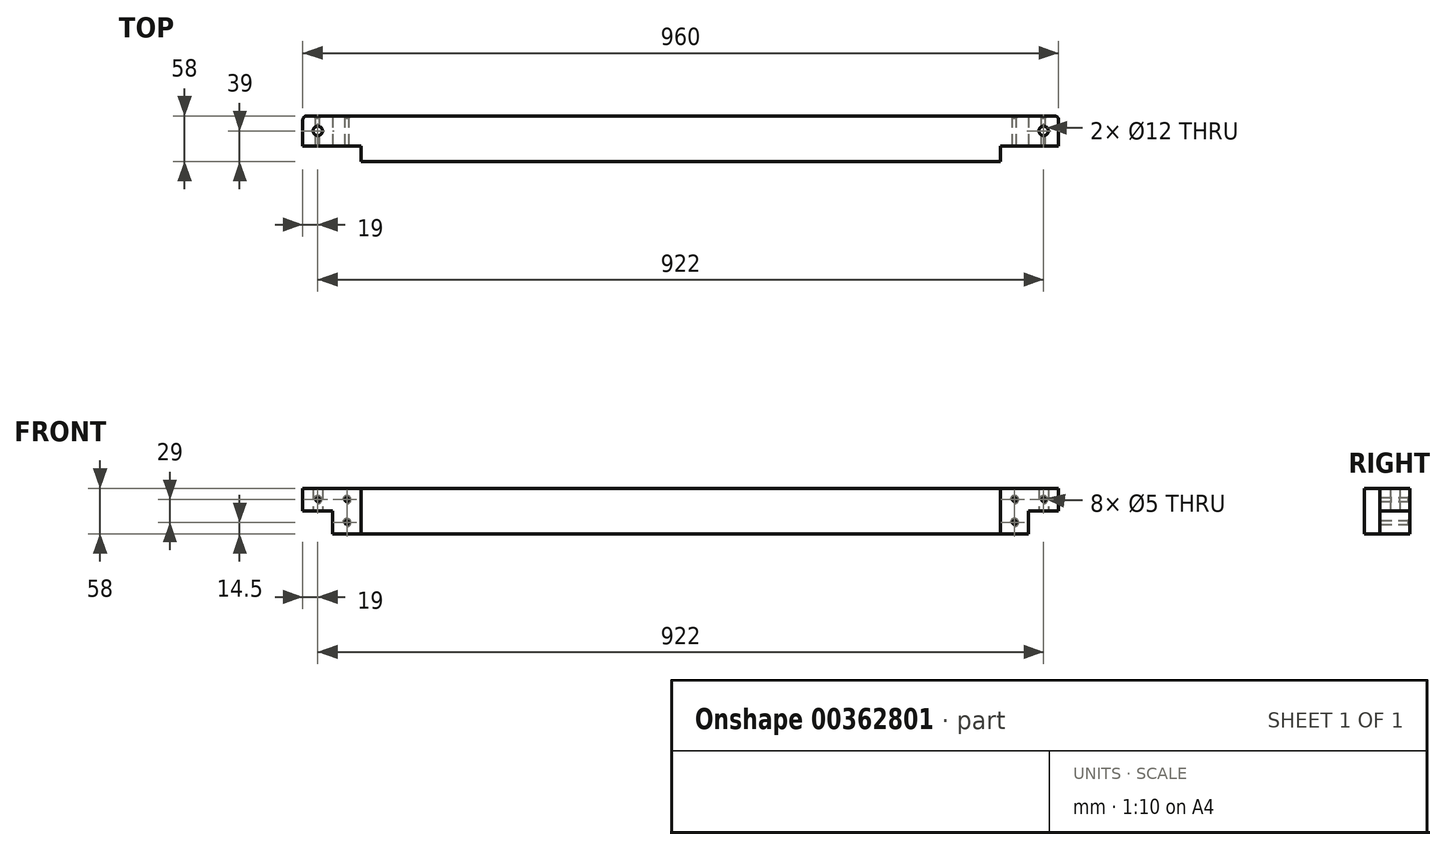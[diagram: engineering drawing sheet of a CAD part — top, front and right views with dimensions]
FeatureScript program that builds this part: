
annotation { "Feature Type Name" : "Feature", "Feature Type Description" : "" }
export const myFeature = defineFeature(function(context is Context, id is Id, definition is map)
    precondition{}
    {
        {
            var Q0;
            Q0=qCreatedBy(makeId("Right.planeOp"),FACE);
            var sketch = newSketch(context, id + "F0", { "sketchPlane" : qUnion([Q0])});
            skLineSegment(sketch, "E0.bottom", {"start": v(29, 29) * mm, "end": v(-29, 29) * mm});
            skLineSegment(sketch, "E0.top", {"start": v(29, -29) * mm, "end": v(-29, -29) * mm});
            skLineSegment(sketch, "E0.left", {"start": v(29, 29) * mm, "end": v(29, -29) * mm});
            skLineSegment(sketch, "E0.right", {"start": v(-29, 29) * mm, "end": v(-29, -29) * mm});
            skPoint(sketch, "E0.middle", {"position": v(0, 0) * mm});
            skLineSegment(sketch, "E1", {"start": v(-9, 29) * mm, "end": v(-9, -29) * mm});
            skLineSegment(sketch, "E2", {"start": v(29, 0) * mm, "end": v(-9, 0) * mm});
            skSolve(sketch);
        }
        {
            var Q0;
            {var subQ5=sQuery(id+"F0.wireOp",EDGE,"E2");Q0=makeQuery(id+"F0.imprint","IMPRINT",FACE,{"disambiguationData":[TD([[makeQuery(id+"F0.imprint","IMPRINT",EDGE,{"derivedFrom":subQ5}),1.0]])]});}
            var Q1;
            {var subQ5=sQuery(id+"F0.wireOp",EDGE,"E2");Q1=makeQuery(id+"F0.imprint","IMPRINT",FACE,{"disambiguationData":[TD([[makeQuery(id+"F0.imprint","IMPRINT",EDGE,{"derivedFrom":subQ5}),-1.0]])]});}
            var Q2;
            {var subQ4=sQuery(id+"F0.wireOp",EDGE,"E0.right");Q2=makeQuery(id+"F0.imprint","IMPRINT",FACE,{"disambiguationData":[TD([[makeQuery(id+"F0.imprint","IMPRINT",EDGE,{"derivedFrom":subQ4}),1.0]])]});}
            extrude(context, id + "F1", {"entities" : qUnion([Q0, Q1, Q2]), "oppositeDirection" : true, "depth" : 480 * mm});
        }
        {
            var Q0;
            {var subQ4=sQuery(id+"F0.wireOp",EDGE,"E0.right");Q0=makeQuery(id+"F0.imprint","IMPRINT",FACE,{"disambiguationData":[TD([[makeQuery(id+"F0.imprint","IMPRINT",EDGE,{"derivedFrom":subQ4}),1.0]])]});}
            extrude(context, id + "F2", {"entities" : qUnion([Q0]), "operationType" : NewBodyOperationType.REMOVE, "oppositeDirection" : true, "depth" : 74 * mm});
        }
        {
            var Q0;
            {var subQ5=sQuery(id+"F0.wireOp",EDGE,"E2");Q0=makeQuery(id+"F0.imprint","IMPRINT",FACE,{"disambiguationData":[TD([[makeQuery(id+"F0.imprint","IMPRINT",EDGE,{"derivedFrom":subQ5}),1.0]])]});}
            extrude(context, id + "F3", {"entities" : qUnion([Q0]), "operationType" : NewBodyOperationType.REMOVE, "oppositeDirection" : true, "depth" : 38 * mm});
        }
        {
            var Q0;
            Q0=makeQuery(id+"F1.opExtrude","CAP_EDGE",EDGE,{"disambiguationData":[OSD([sQuery(id+"F0.wireOp",EDGE,"E0.left")])],"isStart":true});
            fillet(context, id + "F4", {"entities" : qUnion([Q0]), "radius" : 5 * mm, "tangentPropagation" : true, "allowEdgeOverflow" : false});
        }
        {
            var Q0;
            Q0=makeQuery(id+"F3.boolean.opBoolean","COPY",FACE,{"derivedFrom":makeQuery(id+"F3.opExtrude","SWEPT_FACE",FACE,{"disambiguationData":[OSD([sQuery(id+"F0.wireOp",EDGE,"E2")])]})});
            var sketch = newSketch(context, id + "F5", { "sketchPlane" : qUnion([Q0])});
            skPoint(sketch, "E3", {"position": v(-19, -10) * mm});
            skSolve(sketch);
        }
        {
            var Q0;
            Q0=makeQuery(id+"F1.opExtrude","SWEPT_FACE",FACE,{"disambiguationData":[OSD([sQuery(id+"F0.wireOp",EDGE,"E0.left")])]});
            var sketch = newSketch(context, id + "F6", { "sketchPlane" : qUnion([Q0])});
            skPoint(sketch, "E4", {"position": v(19, 14.5) * mm});
            skPoint(sketch, "E5", {"position": v(56, 14.5) * mm});
            skPoint(sketch, "E6", {"position": v(56, -14.5) * mm});
            skSolve(sketch);
        }
        {
            var Q0;
            Q0=sQuery(id+"F5.wireOp",VERTEX,"E3");
            var Q1;
            Q1=makeQuery(id+"F1.opExtrude","SWEPT_BODY",BODY,{"disambiguationData":[OSD([sQuery(id+"F0.wireOp",EDGE,"E0.bottom"),sQuery(id+"F0.wireOp",EDGE,"E0.top"),sQuery(id+"F0.wireOp",EDGE,"E0.left"),sQuery(id+"F0.wireOp",EDGE,"E0.right")])]});
            hole(context, id + "F7", {"style" : HoleStyle.SIMPLE, "endStyle" : HoleEndStyle.THROUGH, "holeDiameter" : 12 * mm, "isTappedThrough" : true, "tappedDepth" : 12 * mm, "tapClearance" : 3, "locations" : qUnion([Q0]), "scope" : qUnion([Q1])});
        }
        {
            var Q0;
            Q0=sQuery(id+"F6.wireOp",VERTEX,"E4");
            var Q1;
            Q1=sQuery(id+"F6.wireOp",VERTEX,"E5");
            var Q2;
            Q2=sQuery(id+"F6.wireOp",VERTEX,"E6");
            var Q3;
            Q3=makeQuery(id+"F1.opExtrude","SWEPT_BODY",BODY,{"disambiguationData":[OSD([sQuery(id+"F0.wireOp",EDGE,"E0.bottom"),sQuery(id+"F0.wireOp",EDGE,"E0.top"),sQuery(id+"F0.wireOp",EDGE,"E0.left"),sQuery(id+"F0.wireOp",EDGE,"E0.right")])]});
            hole(context, id + "F8", {"style" : HoleStyle.C_SINK, "endStyle" : HoleEndStyle.THROUGH, "holeDiameter" : 5 * mm, "cSinkDiameter" : 10 * mm, "cSinkAngle" : 90 * degree, "isTappedThrough" : true, "tappedDepth" : 12 * mm, "tapClearance" : 3, "locations" : qUnion([Q0, Q1, Q2]), "scope" : qUnion([Q3])});
        }
        {
            var Q0;
            Q0=makeQuery(id+"F1.opExtrude","SWEPT_BODY",BODY,{"disambiguationData":[OSD([sQuery(id+"F0.wireOp",EDGE,"E0.bottom"),sQuery(id+"F0.wireOp",EDGE,"E0.top"),sQuery(id+"F0.wireOp",EDGE,"E0.left"),sQuery(id+"F0.wireOp",EDGE,"E0.right")])]});
            var Q1;
            Q1=makeQuery(id+"F1.opExtrude","CAP_FACE",FACE,{"disambiguationData":[OSD([sQuery(id+"F0.wireOp",EDGE,"E0.bottom"),sQuery(id+"F0.wireOp",EDGE,"E0.top"),sQuery(id+"F0.wireOp",EDGE,"E0.left"),sQuery(id+"F0.wireOp",EDGE,"E0.right")])],"isStart":false});
            mirror(context, id + "F9", {"operationType" : NewBodyOperationType.ADD, "entities" : qUnion([Q0]), "mirrorPlane" : qUnion([Q1])});
        }
    });
